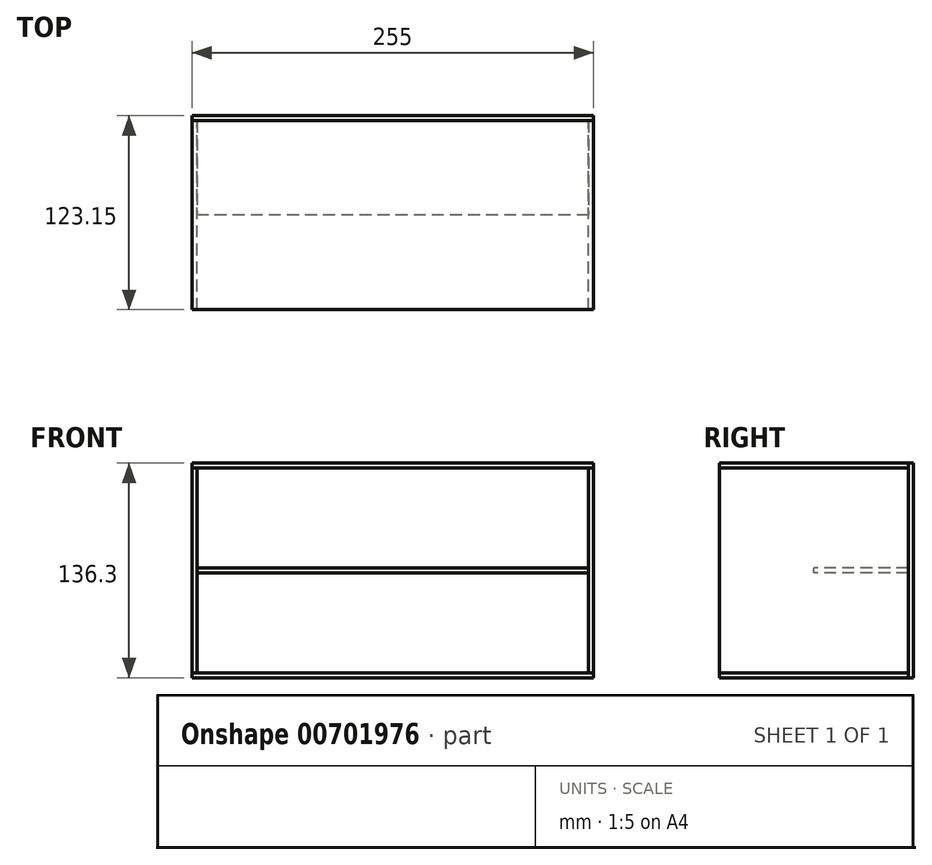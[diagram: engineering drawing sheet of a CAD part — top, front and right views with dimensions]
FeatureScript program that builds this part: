
annotation { "Feature Type Name" : "Feature", "Feature Type Description" : "" }
export const myFeature = defineFeature(function(context is Context, id is Id, definition is map)
    precondition{}
    {
        {
            assignVariable(context, id + "F0", {"name" : "x", "anyValue" : 3.15});
        }
        {
            var Q0;
            Q0=qCreatedBy(makeId("Top.planeOp"),FACE);
            var sketch = newSketch(context, id + "F1", { "sketchPlane" : qUnion([Q0])});
            skLineSegment(sketch, "E0.bottom", {"start": v(0, 0) * mm, "end": v(255, 0) * mm});
            skLineSegment(sketch, "E0.top", {"start": v(0, 120) * mm, "end": v(255, 120) * mm});
            skLineSegment(sketch, "E0.left", {"start": v(0, 0) * mm, "end": v(0, 120) * mm});
            skLineSegment(sketch, "E0.right", {"start": v(255, 0) * mm, "end": v(255, 120) * mm});
            skSolve(sketch);
        }
        {
            var Q0;
            Q0=qSketchRegion(id+"F1",true);
            extrude(context, id + "F2", {"entities" : qUnion([Q0]), "depth" : (getVariable(context, 'x')) * mm, "offsetDistance" : 25 * mm});
        }
        {
            var Q0;
            Q0=makeQuery(id+"F2.opExtrude","SWEPT_FACE",FACE,{"disambiguationData":[OSD([sQuery(id+"F1.wireOp",EDGE,"E0.left")])]});
            var sketch = newSketch(context, id + "F3", { "sketchPlane" : qUnion([Q0])});
            skLineSegment(sketch, "E1.top", {"start": v(0, 133.15) * mm, "end": v(-120, 133.15) * mm});
            skLineSegment(sketch, "E1.left", {"start": v(0, 3.15) * mm, "end": v(0, 133.15) * mm});
            skLineSegment(sketch, "E2", {"start": v(0, 3.15) * mm, "end": v(-120, 3.15) * mm});
            skLineSegment(sketch, "E3", {"start": v(-120, 3.15) * mm, "end": v(-120, 133.15) * mm});
            skSolve(sketch);
        }
        {
            var Q0;
            Q0=qSketchRegion(id+"F3",true);
            extrude(context, id + "F4", {"entities" : qUnion([Q0]), "oppositeDirection" : true, "depth" : (getVariable(context, 'x')) * mm, "offsetDistance" : 25 * mm});
        }
        {
            var Q0;
            Q0=makeQuery(id+"FVTuVMvbx6C6lcW_2.boolean.opBoolean","MERGE",FACE,{"derivedFrom":[makeQuery(id+"F4.opExtrude","SWEPT_FACE",FACE,{"disambiguationData":[OSD([sQuery(id+"F3.wireOp",EDGE,"E1.left")])]}),makeQuery(id+"FVTuVMvbx6C6lcW_2.opExtrude","SWEPT_FACE",FACE,{"disambiguationData":[OSD([sQuery(id+"F9WBSx8lvzqTq6O_2.wireOp",EDGE,"DdJYWYcg-8VXy-0sGO-iMAo-MInbchsGbsPU")])]})]});
            var sketch = newSketch(context, id + "F5", { "sketchPlane" : qUnion([Q0])});
            skLineSegment(sketch, "E4.bottom", {"start": v(3.15, 69.72) * mm, "end": v(251.85, 69.72) * mm});
            skLineSegment(sketch, "E4.top", {"start": v(3.15, 66.57) * mm, "end": v(251.85, 66.57) * mm});
            skLineSegment(sketch, "E4.right", {"start": v(251.85, 69.72) * mm, "end": v(251.85, 66.57) * mm});
            skLineSegment(sketch, "E5", {"start": v(251.85, 3.15) * mm, "end": v(251.85, 66.57) * mm, "construction": true});
            skLineSegment(sketch, "E6", {"start": v(3.15, 66.57) * mm, "end": v(3.15, 69.72) * mm});
            skPoint(sketch, "E7", {"position": v(3.15, 68.15) * mm});
            skSolve(sketch);
        }
        {
            var Q0;
            Q0=qSketchRegion(id+"F5",true);
            var Q1;
            Q1=makeQuery(id+"F4.opExtrude","SWEPT_FACE",FACE,{"disambiguationData":[OSD([sQuery(id+"F3.wireOp",EDGE,"E3")])]});
            extrude(context, id + "F6", {"entities" : qUnion([Q0]), "endBound" : BoundingType.UP_TO_SURFACE, "oppositeDirection" : true, "depth" : 25 * mm, "endBoundEntityFace" : qUnion([Q1]), "offsetDistance" : 25 * mm});
        }
        {
            var Q0;
            Q0=makeQuery(id+"F2.opExtrude","SWEPT_BODY",BODY,{"disambiguationData":[OSD([sQuery(id+"F1.wireOp",EDGE,"E0.bottom"),sQuery(id+"F1.wireOp",EDGE,"E0.top"),sQuery(id+"F1.wireOp",EDGE,"E0.left"),sQuery(id+"F1.wireOp",EDGE,"E0.right")])]});
            transform(context, id + "F7", {"entities" : qUnion([Q0]), "transformType" : TransformType.TRANSLATION_3D, "dx" : 0 * mm, "dy" : 0 * mm, "dz" : 133.15 * mm, "makeCopy" : true});
        }
        {
            var Q0;
            Q0=makeQuery(id+"F4.opExtrude","SWEPT_BODY",BODY,{"disambiguationData":[OSD([sQuery(id+"F3.wireOp",EDGE,"E1.top"),sQuery(id+"F3.wireOp",EDGE,"E1.left"),sQuery(id+"F3.wireOp",EDGE,"E2"),sQuery(id+"F3.wireOp",EDGE,"E3")])]});
            transform(context, id + "F8", {"entities" : qUnion([Q0]), "transformType" : TransformType.TRANSLATION_3D, "dx" : (263.7 + 3.15 - 15) * mm, "dy" : 0 * mm, "dz" : 0 * mm, "makeCopy" : true});
        }
        {
            var Q0;
            Q0=makeQuery(id+"F7.opPattern","COPY",FACE,{"derivedFrom":makeQuery(id+"F2.opExtrude","SWEPT_FACE",FACE,{"disambiguationData":[OSD([sQuery(id+"F1.wireOp",EDGE,"E0.top")])]}),"instanceName":"1"});
            var sketch = newSketch(context, id + "F9", { "sketchPlane" : qUnion([Q0])});
            skLineSegment(sketch, "E8.bottom", {"start": v(-255, 136.3) * mm, "end": v(0, 136.3) * mm});
            skLineSegment(sketch, "E8.top", {"start": v(-255, 0) * mm, "end": v(0, 0) * mm});
            skLineSegment(sketch, "E8.left", {"start": v(-255, 136.3) * mm, "end": v(-255, 0) * mm});
            skLineSegment(sketch, "E8.right", {"start": v(0, 136.3) * mm, "end": v(0, 0) * mm});
            skSolve(sketch);
        }
        {
            var Q0;
            Q0=qSketchRegion(id+"F9",true);
            extrude(context, id + "F10", {"entities" : qUnion([Q0]), "depth" : (getVariable(context, 'x')) * mm, "offsetDistance" : 25 * mm});
        }
        {
            var Q0;
            Q0=makeQuery(id+"F6.opExtrude","SWEPT_FACE",FACE,{"disambiguationData":[OSD([sQuery(id+"F5.wireOp",EDGE,"E4.bottom")])]});
            var sketch = newSketch(context, id + "F11", { "sketchPlane" : qUnion([Q0])});
            skLineSegment(sketch, "E9.bottom", {"start": v(3.15, 60) * mm, "end": v(251.85, 60) * mm});
            skLineSegment(sketch, "E9.top", {"start": v(3.15, 0) * mm, "end": v(251.85, 0) * mm});
            skLineSegment(sketch, "E9.left", {"start": v(3.15, 60) * mm, "end": v(3.15, 0) * mm});
            skLineSegment(sketch, "E9.right", {"start": v(251.85, 60) * mm, "end": v(251.85, 0) * mm});
            skSolve(sketch);
        }
        {
            var Q0;
            Q0 = qSketchRegion(id + "F11", true);
            extrude(context, id + "F12", {"entities" : qUnion([Q0]), "operationType" : NewBodyOperationType.REMOVE, "oppositeDirection" : true, "depth" : 25 * mm, "offsetDistance" : 25 * mm});
        }
    });
